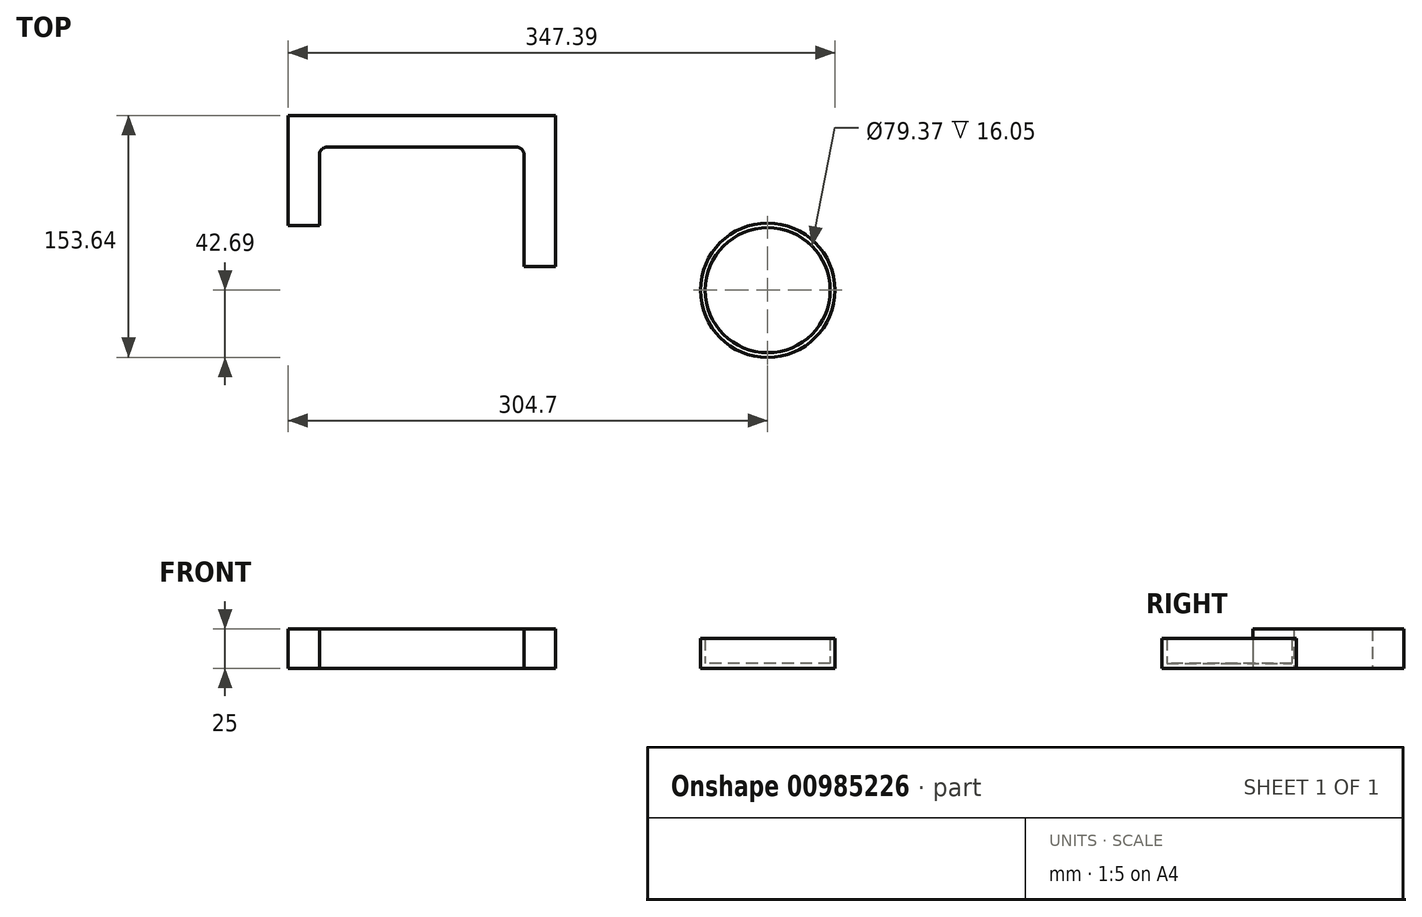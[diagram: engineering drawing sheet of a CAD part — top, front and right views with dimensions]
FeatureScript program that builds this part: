
annotation { "Feature Type Name" : "Feature", "Feature Type Description" : "" }
export const myFeature = defineFeature(function(context is Context, id is Id, definition is map)
    precondition{}
    {
        {
            var Q0;
            Q0=qCreatedBy(makeId("Top.planeOp"),FACE);
            var sketch = newSketch(context, id + "F0", { "sketchPlane" : qUnion([Q0])});
            skCircle(sketch, "E0", {"center": v(0, 0) * mm, "radius": 39.69 * mm});
            skCircle(sketch, "E1", {"center": v(0, 0) * mm, "radius": 42.69 * mm});
            skSolve(sketch);
        }
        {
            var Q0;
            Q0=makeQuery(id+"F0.imprint","IMPRINT",FACE,{"disambiguationData":[TD([[makeQuery(id+"F0.imprint","IMPRINT",EDGE,{"derivedFrom":sQuery(id+"F0.wireOp",EDGE,"E0")}),1.0]])]});
            var Q1;
            Q1=makeQuery(id+"F0.imprint","IMPRINT",FACE,{"disambiguationData":[TD([[makeQuery(id+"F0.imprint","IMPRINT",EDGE,{"derivedFrom":sQuery(id+"F0.wireOp",EDGE,"E0")}),-1.0]])]});
            extrude(context, id + "F1", {"entities" : qUnion([Q0, Q1]), "depth" : 3 * mm, "offsetDistance" : 25 * mm});
        }
        {
            var Q0;
            Q0 = qSketchRegion(id + "F0", true);
            extrude(context, id + "F2", {"entities" : qUnion([Q0]), "operationType" : NewBodyOperationType.ADD, "depth" : 19.05 * mm, "offsetDistance" : 25 * mm});
        }
        {
            var Q0;
            Q0=qCreatedBy(makeId("Top.planeOp"),FACE);
            var sketch = newSketch(context, id + "F3", { "sketchPlane" : qUnion([Q0])});
            skLineSegment(sketch, "E2", {"start": v(-126.1, -107.35) * mm, "end": v(-126.1, -57.35) * mm});
            skLineSegment(sketch, "E3", {"start": v(-126.1, -57.35) * mm, "end": v(0.9, -57.35) * mm});
            skLineSegment(sketch, "E4", {"start": v(0.9, -57.35) * mm, "end": v(0.9, -133.35) * mm});
            skLineSegment(sketch, "E5", {"start": v(-126.1, -107.35) * mm, "end": v(-146.1, -107.35) * mm});
            skLineSegment(sketch, "E6", {"start": v(-146.1, -107.35) * mm, "end": v(-146.1, -57.35) * mm});
            skLineSegment(sketch, "E7", {"start": v(-146.1, -57.35) * mm, "end": v(-146.1, -37.35) * mm});
            skLineSegment(sketch, "E8", {"start": v(-146.1, -37.35) * mm, "end": v(20.9, -37.35) * mm});
            skLineSegment(sketch, "E9", {"start": v(20.9, -37.35) * mm, "end": v(20.9, -133.35) * mm});
            skLineSegment(sketch, "E10", {"start": v(0.9, -133.35) * mm, "end": v(20.9, -133.35) * mm});
            skLineSegment(sketch, "E11", {"start": v(-284.7, 40.95) * mm, "end": v(-284.7, 90.95) * mm});
            skLineSegment(sketch, "E12", {"start": v(-284.7, 90.95) * mm, "end": v(-154.7, 90.95) * mm});
            skLineSegment(sketch, "E13", {"start": v(-154.7, 90.95) * mm, "end": v(-154.7, 14.95) * mm});
            skLineSegment(sketch, "E14", {"start": v(-284.7, 40.95) * mm, "end": v(-304.7, 40.95) * mm});
            skLineSegment(sketch, "E15", {"start": v(-304.7, 40.95) * mm, "end": v(-304.7, 90.95) * mm});
            skLineSegment(sketch, "E16", {"start": v(-304.7, 90.95) * mm, "end": v(-304.7, 110.95) * mm});
            skLineSegment(sketch, "E17", {"start": v(-304.7, 110.95) * mm, "end": v(-134.7, 110.95) * mm});
            skLineSegment(sketch, "E18", {"start": v(-134.7, 110.95) * mm, "end": v(-134.7, 14.95) * mm});
            skLineSegment(sketch, "E19", {"start": v(-154.7, 14.95) * mm, "end": v(-134.7, 14.95) * mm});
            skSolve(sketch);
        }
        {
            var Q0;
            Q0=makeQuery(id+"F3.imprint","IMPRINT",FACE,{"disambiguationData":[TD([[makeQuery(id+"F3.imprint","IMPRINT",EDGE,{"derivedFrom":sQuery(id+"F3.wireOp",EDGE,"E11")}),1.0]])]});
            extrude(context, id + "F4", {"entities" : qUnion([Q0]), "operationType" : NewBodyOperationType.ADD, "depth" : 25 * mm, "offsetDistance" : 25 * mm});
        }
        {
            var Q0;
            Q0=makeQuery(id+"F4.opExtrude","SWEPT_EDGE",EDGE,{"disambiguationData":[OSD([sQuery(id+"F3.wireOp",EDGE,"E11"),sQuery(id+"F3.wireOp",EDGE,"E12")])]});
            var Q1;
            Q1=makeQuery(id+"F4.opExtrude","SWEPT_EDGE",EDGE,{"disambiguationData":[OSD([sQuery(id+"F3.wireOp",EDGE,"E12"),sQuery(id+"F3.wireOp",EDGE,"E13")])]});
            fillet(context, id + "F5", {"entities" : qUnion([Q0, Q1]), "radius" : 5 * mm, "tangentPropagation" : true, "allowEdgeOverflow" : false});
        }
    });
